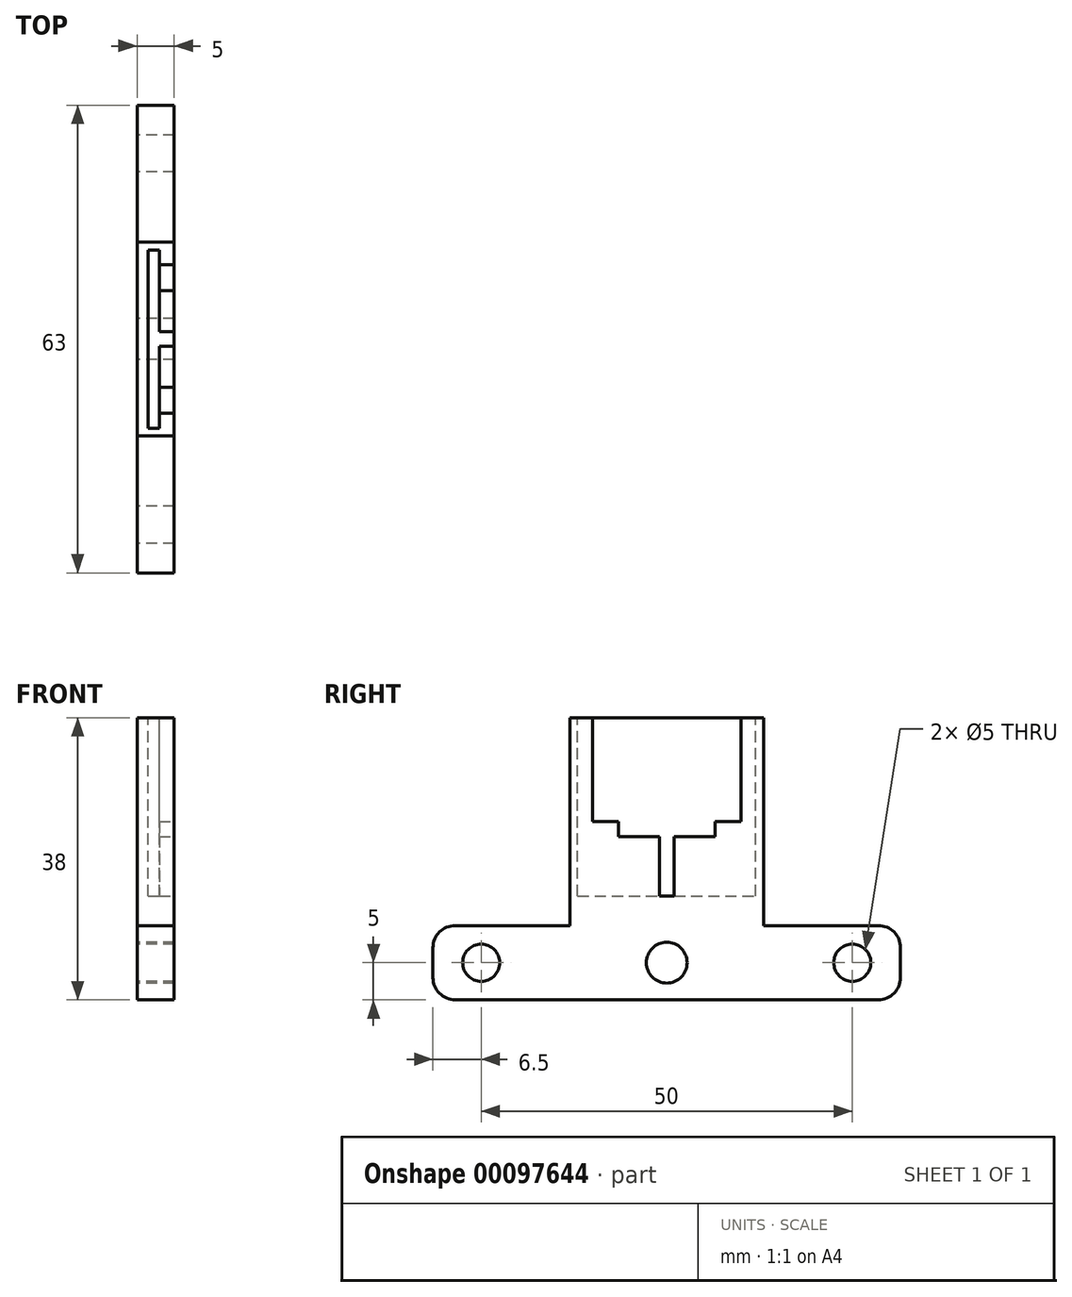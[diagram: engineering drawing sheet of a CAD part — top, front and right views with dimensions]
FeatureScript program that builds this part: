
annotation { "Feature Type Name" : "Feature", "Feature Type Description" : "" }
export const myFeature = defineFeature(function(context is Context, id is Id, definition is map)
    precondition{}
    {
        {
            var Q0;
            Q0=qCreatedBy(makeId("Right.planeOp"),FACE);
            var sketch = newSketch(context, id + "F0", { "sketchPlane" : qUnion([Q0])});
            skLineSegment(sketch, "E0.bottom", {"start": v(28.5, -5) * mm, "end": v(-28.5, -5) * mm});
            skLineSegment(sketch, "E0.top", {"start": v(28.5, 5) * mm, "end": v(-28.5, 5) * mm});
            skLineSegment(sketch, "E0.left", {"start": v(31.5, -2) * mm, "end": v(31.5, 2) * mm});
            skLineSegment(sketch, "E0.right", {"start": v(-31.5, -2) * mm, "end": v(-31.5, 2) * mm});
            skPoint(sketch, "E0.middle", {"position": v(0, 0) * mm});
            skPoint(sketch, "E1.visualSharp", {"position": v(-31.5, -5) * mm});
            skArc(sketch, "E1.filletArc", {"start": v(-31.5, -2) * mm, "mid": v(-30.62, -4.12) * mm, "end": v(-28.5, -5) * mm});
            skPoint(sketch, "E2.visualSharp", {"position": v(31.5, -5) * mm});
            skArc(sketch, "E2.filletArc", {"start": v(28.5, -5) * mm, "mid": v(30.62, -4.12) * mm, "end": v(31.5, -2) * mm});
            skCircle(sketch, "E3", {"center": v(-25, 0) * mm, "radius": 2.5 * mm});
            skCircle(sketch, "E4.MirrorC", {"center": v(25, 0) * mm, "radius": 2.5 * mm});
            skPoint(sketch, "E5.visualSharp", {"position": v(-31.5, 5) * mm});
            skArc(sketch, "E5.filletArc", {"start": v(-28.5, 5) * mm, "mid": v(-30.62, 4.12) * mm, "end": v(-31.5, 2) * mm});
            skPoint(sketch, "E6.visualSharp", {"position": v(31.5, 5) * mm});
            skArc(sketch, "E6.filletArc", {"start": v(31.5, 2) * mm, "mid": v(30.62, 4.12) * mm, "end": v(28.5, 5) * mm});
            skSolve(sketch);
        }
        {
            var Q0;
            Q0=makeQuery(id+"F0.imprint","IMPRINT",FACE,{"disambiguationData":[TD([[makeQuery(id+"F0.imprint","IMPRINT",EDGE,{"derivedFrom":sQuery(id+"F0.wireOp",EDGE,"E0.bottom")}),-1.0]])]});
            extrude(context, id + "F1", {"entities" : qUnion([Q0]), "depth" : 5 * mm});
        }
        {
            var Q0;
            Q0=sQuery(id+"F0.wireOp",VERTEX,"E0.middle");
            var Q1;
            Q1=makeQuery(id+"F1.opExtrude","SWEPT_BODY",BODY,{"disambiguationData":[OSD([sQuery(id+"F0.wireOp",EDGE,"E0.bottom"),sQuery(id+"F0.wireOp",EDGE,"E0.top"),sQuery(id+"F0.wireOp",EDGE,"E0.left"),sQuery(id+"F0.wireOp",EDGE,"E0.right"),sQuery(id+"F0.wireOp",EDGE,"E1.filletArc"),sQuery(id+"F0.wireOp",EDGE,"E2.filletArc"),sQuery(id+"F0.wireOp",EDGE,"E3"),sQuery(id+"F0.wireOp",EDGE,"E4.MirrorC"),sQuery(id+"F0.wireOp",EDGE,"E5.filletArc"),sQuery(id+"F0.wireOp",EDGE,"E6.filletArc")])]});
            hole(context, id + "F2", {"style" : HoleStyle.SIMPLE, "endStyle" : HoleEndStyle.BLIND, "oppositeDirection" : true, "standardTappedOrClearance" : lookupTablePath({ "standard" : "ISO", "fit" : "Normal", "size" : "M5", "type" : "Clearance" }), "standardBlindInLast" : lookupTablePath({ "fit" : "Standard", "standard" : "ISO", "size" : "M5", "type" : "Clearance" }), "holeDiameter" : 5.5 * mm, "holeDepth" : 7 * mm, "locations" : qUnion([Q0]), "scope" : qUnion([Q1])});
        }
        {
            var Q0;
            Q0=qCreatedBy(makeId("Right.planeOp"),FACE);
            var sketch = newSketch(context, id + "F3", { "sketchPlane" : qUnion([Q0])});
            skLineSegment(sketch, "E7", {"start": v(-13.03, 5) * mm, "end": v(-13.03, 33) * mm});
            skLineSegment(sketch, "E8", {"start": v(-13.03, 33) * mm, "end": v(0, 33) * mm});
            skLineSegment(sketch, "E9.MirrorCS", {"start": v(13.03, 33) * mm, "end": v(0, 33) * mm});
            skLineSegment(sketch, "E10.MirrorCS", {"start": v(13.03, 5) * mm, "end": v(13.03, 33) * mm});
            skLineSegment(sketch, "E11", {"start": v(-13.03, 5) * mm, "end": v(13.03, 5) * mm});
            skSolve(sketch);
        }
        {
            var Q0;
            Q0=makeQuery(id+"F3.imprint","IMPRINT",FACE,{"disambiguationData":[TD([[makeQuery(id+"F3.imprint","IMPRINT",EDGE,{"derivedFrom":sQuery(id+"F3.wireOp",EDGE,"E7")}),-1.0]])]});
            var Q1;
            Q1=makeQuery(id+"F1.opExtrude","CAP_FACE",FACE,{"disambiguationData":[OSD([sQuery(id+"F0.wireOp",EDGE,"E0.bottom"),sQuery(id+"F0.wireOp",EDGE,"E0.top"),sQuery(id+"F0.wireOp",EDGE,"E0.left"),sQuery(id+"F0.wireOp",EDGE,"E0.right"),sQuery(id+"F0.wireOp",EDGE,"E1.filletArc"),sQuery(id+"F0.wireOp",EDGE,"E2.filletArc"),sQuery(id+"F0.wireOp",EDGE,"E3"),sQuery(id+"F0.wireOp",EDGE,"E4.MirrorC"),sQuery(id+"F0.wireOp",EDGE,"E5.filletArc"),sQuery(id+"F0.wireOp",EDGE,"E6.filletArc")])],"isStart":false});
            extrude(context, id + "F4", {"entities" : qUnion([Q0]), "operationType" : NewBodyOperationType.ADD, "endBound" : BoundingType.UP_TO_SURFACE, "endBoundEntityFace" : qUnion([Q1]), "depth" : 25 * mm});
        }
        {
            var Q0;
            {var subQ0=sQuery(id+"F0.wireOp",EDGE,"E6.filletArc");var subQ1=sQuery(id+"F0.wireOp",EDGE,"E5.filletArc");var subQ2=sQuery(id+"F0.wireOp",EDGE,"E4.MirrorC");var subQ3=sQuery(id+"F0.wireOp",EDGE,"E3");var subQ4=sQuery(id+"F0.wireOp",EDGE,"E2.filletArc");var subQ5=sQuery(id+"F0.wireOp",EDGE,"E1.filletArc");var subQ6=sQuery(id+"F0.wireOp",EDGE,"E0.right");var subQ7=sQuery(id+"F0.wireOp",EDGE,"E0.left");var subQ8=sQuery(id+"F0.wireOp",EDGE,"E0.top");var subQ9=sQuery(id+"F0.wireOp",EDGE,"E0.bottom");Q0=makeQuery(id+"F4.boolean.opBoolean","MERGE",FACE,{"derivedFrom":[makeQuery(id+"F1.opExtrude","CAP_FACE",FACE,{"disambiguationData":[OSD([subQ9,subQ8,subQ7,subQ6,subQ5,subQ4,subQ3,subQ2,subQ1,subQ0])],"isStart":false}),makeQuery(id+"F4.opExtrude","CAP_FACE",FACE,{"disambiguationData":[OSD([subQ9,subQ8,subQ7,subQ6,subQ5,subQ4,subQ3,subQ2,subQ1,subQ0])],"isStart":false})]});}
            var sketch = newSketch(context, id + "F5", { "sketchPlane" : qUnion([Q0])});
            skLineSegment(sketch, "E12.bottom", {"start": v(-10.02, 33) * mm, "end": v(10.02, 33) * mm});
            skLineSegment(sketch, "E12.top", {"start": v(-10.03, 9) * mm, "end": v(10.03, 9) * mm});
            skLineSegment(sketch, "E12.left", {"start": v(-10.02, 33) * mm, "end": v(-10.03, 9) * mm});
            skLineSegment(sketch, "E12.right", {"start": v(10.03, 33) * mm, "end": v(10.02, 9) * mm});
            skLineSegment(sketch, "E13", {"start": v(-1, 9) * mm, "end": v(-1, 17) * mm});
            skLineSegment(sketch, "E14", {"start": v(-1, 17) * mm, "end": v(-10.02, 17) * mm});
            skLineSegment(sketch, "E15.MirrorCS", {"start": v(1, 9) * mm, "end": v(1, 17) * mm});
            skLineSegment(sketch, "E16.MirrorCS", {"start": v(1, 17) * mm, "end": v(10.02, 17) * mm});
            skLineSegment(sketch, "E17", {"start": v(-6.5, 17) * mm, "end": v(-6.5, 19) * mm});
            skLineSegment(sketch, "E18", {"start": v(-6.5, 19) * mm, "end": v(-10.02, 19) * mm});
            skLineSegment(sketch, "E19.MirrorCS", {"start": v(6.5, 17) * mm, "end": v(6.5, 19) * mm});
            skLineSegment(sketch, "E20.MirrorCS", {"start": v(6.5, 19) * mm, "end": v(10.02, 19) * mm});
            skSolve(sketch);
        }
        {
            var Q0;
            {var subQ1=sQuery(id+"F5.wireOp",EDGE,"E12.bottom");Q0=makeQuery(id+"F5.imprint","IMPRINT",FACE,{"disambiguationData":[TD([[makeQuery(id+"F5.imprint","IMPRINT",EDGE,{"derivedFrom":subQ1}),1.0]])]});}
            extrude(context, id + "F6", {"entities" : qUnion([Q0]), "operationType" : NewBodyOperationType.REMOVE, "oppositeDirection" : true, "depth" : 3.5 * mm});
        }
        {
            var Q0;
            Q0=makeQuery(id+"F4.opExtrude","SWEPT_FACE",FACE,{"disambiguationData":[OSD([sQuery(id+"F3.wireOp",EDGE,"E8"),sQuery(id+"F3.wireOp",EDGE,"E9.MirrorCS")])]});
            var sketch = newSketch(context, id + "F7", { "sketchPlane" : qUnion([Q0])});
            skLineSegment(sketch, "E21", {"start": v(1.5, 0) * mm, "end": v(1.5, -12) * mm});
            skLineSegment(sketch, "E22", {"start": v(1.5, -12) * mm, "end": v(3, -12) * mm});
            skLineSegment(sketch, "E23", {"start": v(3, -12) * mm, "end": v(3, 0) * mm});
            skLineSegment(sketch, "E24.MirrorCS", {"start": v(1.5, 0) * mm, "end": v(1.5, 12) * mm});
            skLineSegment(sketch, "E25.MirrorCS", {"start": v(1.5, 12) * mm, "end": v(3, 12) * mm});
            skLineSegment(sketch, "E26.MirrorCS", {"start": v(3, 12) * mm, "end": v(3, 0) * mm});
            skSolve(sketch);
        }
        {
            var Q0;
            {var subQ0=sQuery(id+"F7.wireOp",EDGE,"E24.MirrorCS");var subQ16=sQuery(id+"F7.wireOp",EDGE,"E21");var subQ17=makeQuery(id+"F7.imprint","INTERSECT",VERTEX,{"derivedFrom":[subQ16,subQ0]});Q0=makeQuery(id+"F7.imprint","IMPRINT",FACE,{"disambiguationData":[TD([[makeQuery(id+"F7.imprint","IMPRINT",EDGE,{"disambiguationData":[TD([[subQ17,-1.0]])],"derivedFrom":subQ16}),1.0]])]});}
            var Q1;
            {var subQ3=sQuery(id+"F7.wireOp",EDGE,"E25.MirrorCS");Q1=makeQuery(id+"F7.imprint","IMPRINT",FACE,{"disambiguationData":[TD([[makeQuery(id+"F7.imprint","IMPRINT",EDGE,{"derivedFrom":subQ3}),-1.0]])]});}
            var Q2;
            {var subQ3=sQuery(id+"F7.wireOp",EDGE,"E22");Q2=makeQuery(id+"F7.imprint","IMPRINT",FACE,{"disambiguationData":[TD([[makeQuery(id+"F7.imprint","IMPRINT",EDGE,{"derivedFrom":subQ3}),1.0]])]});}
            var Q3;
            Q3=makeQuery(id+"F6.boolean.opBoolean","COPY",FACE,{"derivedFrom":makeQuery(id+"F6.opExtrude","SWEPT_FACE",FACE,{"disambiguationData":[OSD([sQuery(id+"F5.wireOp",EDGE,"E12.top")])]})});
            extrude(context, id + "F8", {"entities" : qUnion([Q0, Q1, Q2]), "operationType" : NewBodyOperationType.REMOVE, "endBound" : BoundingType.UP_TO_SURFACE, "oppositeDirection" : true, "endBoundEntityFace" : qUnion([Q3]), "depth" : 25 * mm});
        }
    });
